# Revit family: Accessory-Towel_Bar-KOHLER-Complementary-K-5630IN_1
name_source: partatom
category: Specialty Equipment
revit_build: Autodesk Revit 2017 (Build: 20160225_1515(x64)
units: mm (PartAtom-declared; Revit-internal decimal feet)

## family parameters
Cut with Voids When Loaded = No
Host = Face
OmniClass Number = 23.31.25.00
Part Type = Normal
Room Calculation Point = No
Round Connector Dimension = Use Diameter
Shared = No

## types (2) — shared parameters
ADA Compliant = No
Assembly Code = C1030200
Date Modified = 09/04/2020
Default Elevation = 42"
Description = 610 mm Towel Bar
Height = 1 3/4"
Length = 2 13/16"
Manufacturer = KOHLER Co.
Master Format 2014 = 10 28 00
Master Format 2014 Name = Toilet, Bath, and Laundry Accessories
Material = Premium Metal Construction
Product Documentation Link = http://resources.kohler.com
Product Name = Complementary
Product Page URL = https://www.kohler.co.in
URL = https://www.kohler.co.in
WaterSense Certified = No
Width = 24"

## per-type parameters (varying)
| type | Finish | Model | Type |
| CP-Polished Chrome | Kohler-Metal-CP-Polished_Chrome | K-5630IN-CP | 1 |
| AF-Flange Gold | Kohler-Metal-AF-Flange_Gold | K-5630IN-AF | 2 |

## geometry (parser evidence)
native form markers: Sweep x5
no freeform markers — native parametric forms only
